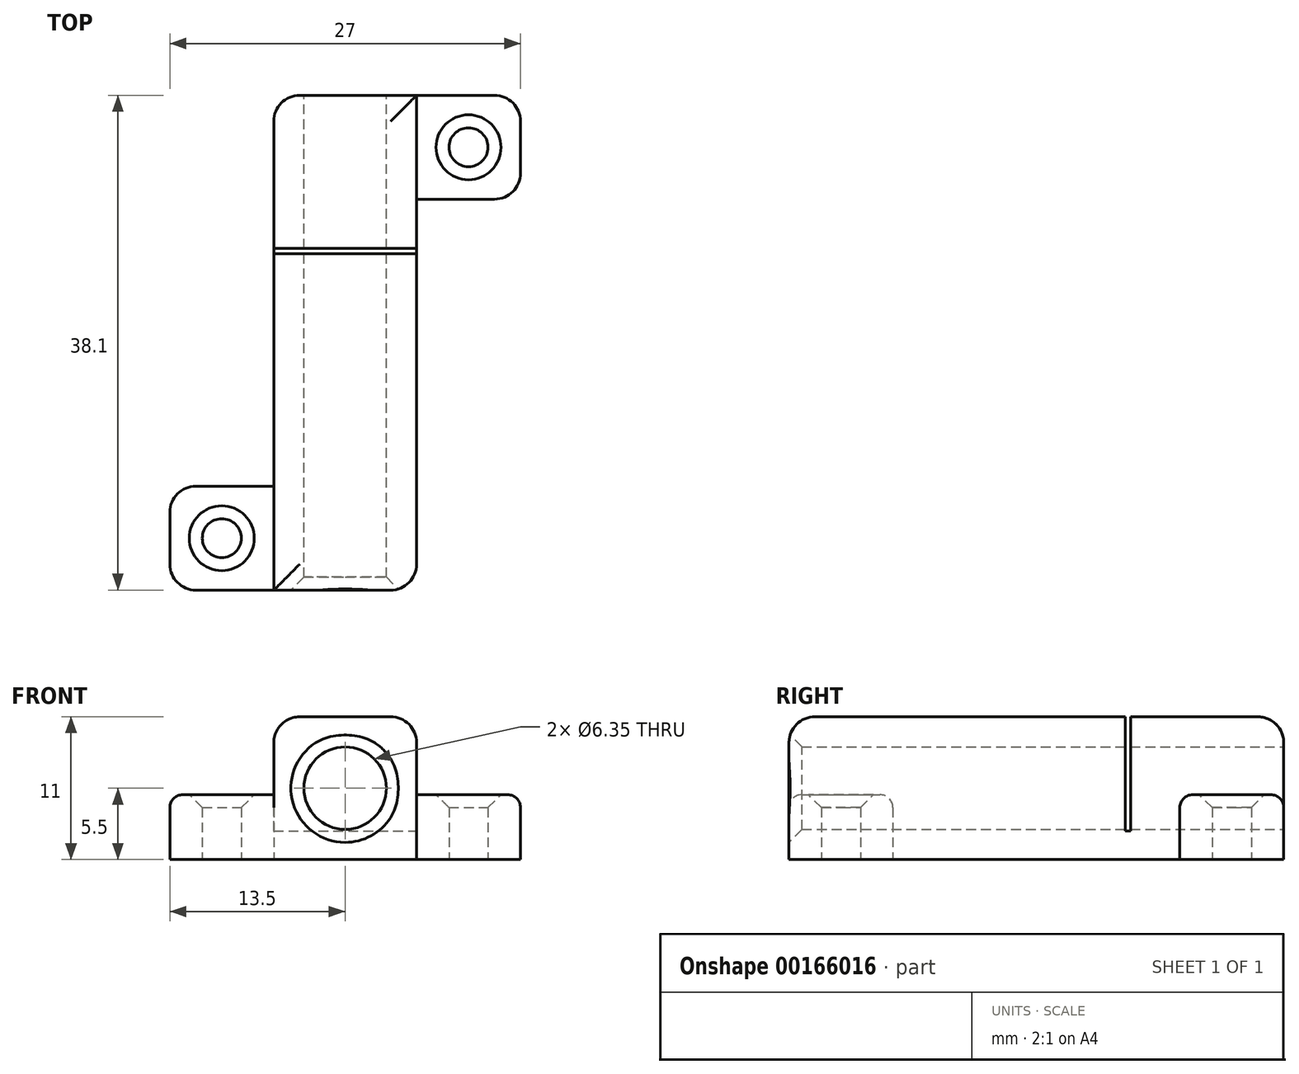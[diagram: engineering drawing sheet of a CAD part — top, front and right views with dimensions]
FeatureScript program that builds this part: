
annotation { "Feature Type Name" : "Feature", "Feature Type Description" : "" }
export const myFeature = defineFeature(function(context is Context, id is Id, definition is map)
    precondition{}
    {
        {
            var Q0;
            Q0=qCreatedBy(makeId("Front.planeOp"),FACE);
            var sketch = newSketch(context, id + "F0", { "sketchPlane" : qUnion([Q0])});
            skLineSegment(sketch, "E0.bottom", {"start": v(-5.5, 0) * mm, "end": v(5.5, 0) * mm});
            skLineSegment(sketch, "E0.top", {"start": v(-5.5, 11) * mm, "end": v(5.5, 11) * mm});
            skLineSegment(sketch, "E0.left", {"start": v(-5.5, 0) * mm, "end": v(-5.5, 11) * mm});
            skLineSegment(sketch, "E0.right", {"start": v(5.5, 0) * mm, "end": v(5.5, 11) * mm});
            skCircle(sketch, "E1", {"center": v(0, 5.5) * mm, "radius": 3.18 * mm});
            skLineSegment(sketch, "E2", {"start": v(0, 11) * mm, "end": v(0, 5.5) * mm, "construction": true});
            skLineSegment(sketch, "E3", {"start": v(5.5, 5.5) * mm, "end": v(0, 5.5) * mm, "construction": true});
            skSolve(sketch);
        }
        {
            var Q0;
            Q0=makeQuery(id+"F0.imprint","IMPRINT",FACE,{"disambiguationData":[TD([[makeQuery(id+"F0.imprint","IMPRINT",EDGE,{"derivedFrom":sQuery(id+"F0.wireOp",EDGE,"E0.bottom")}),1.0]])]});
            extrude(context, id + "F1", {"entities" : qUnion([Q0]), "depth" : 38.1 * mm});
        }
        {
            var Q0;
            Q0=makeQuery(id+"F1.opExtrude","SWEPT_FACE",FACE,{"disambiguationData":[OSD([sQuery(id+"F0.wireOp",EDGE,"E0.bottom")])]});
            var sketch = newSketch(context, id + "F2", { "sketchPlane" : qUnion([Q0])});
            skLineSegment(sketch, "E4.0.0", {"start": v(-5.5, 0) * mm, "end": v(5.5, 0) * mm});
            skLineSegment(sketch, "E4.0.1", {"start": v(5.5, 0) * mm, "end": v(5.5, 38.1) * mm});
            skLineSegment(sketch, "E4.0.2", {"start": v(5.5, 38.1) * mm, "end": v(-5.5, 38.1) * mm});
            skLineSegment(sketch, "E4.0.3", {"start": v(-5.5, 38.1) * mm, "end": v(-5.5, 0) * mm});
            skLineSegment(sketch, "E5.bottom", {"start": v(-5.5, 38.1) * mm, "end": v(-13.5, 38.1) * mm});
            skLineSegment(sketch, "E5.top", {"start": v(-5.5, 30.1) * mm, "end": v(-13.5, 30.1) * mm});
            skLineSegment(sketch, "E5.left", {"start": v(-5.5, 38.1) * mm, "end": v(-5.5, 30.1) * mm});
            skLineSegment(sketch, "E5.right", {"start": v(-13.5, 38.1) * mm, "end": v(-13.5, 30.1) * mm});
            skLineSegment(sketch, "E6.bottom", {"start": v(5.5, 0) * mm, "end": v(13.5, 0) * mm});
            skLineSegment(sketch, "E6.top", {"start": v(5.5, 8) * mm, "end": v(13.5, 8) * mm});
            skLineSegment(sketch, "E6.left", {"start": v(5.5, 0) * mm, "end": v(5.5, 8) * mm});
            skLineSegment(sketch, "E6.right", {"start": v(13.5, 0) * mm, "end": v(13.5, 8) * mm});
            skCircle(sketch, "E7", {"center": v(-9.5, 34.1) * mm, "radius": 1.5 * mm});
            skPoint(sketch, "E7.centerSnap0", {"position": v(-5.5, 34.1) * mm});
            skCircle(sketch, "E8", {"center": v(9.5, 4) * mm, "radius": 1.5 * mm});
            skPoint(sketch, "E8.centerSnap0", {"position": v(9.5, 8) * mm});
            skLineSegment(sketch, "E9", {"start": v(9.5, 8) * mm, "end": v(9.5, 4) * mm, "construction": true});
            skLineSegment(sketch, "E10", {"start": v(13.5, 4) * mm, "end": v(9.5, 4) * mm, "construction": true});
            skPoint(sketch, "E10.startSnap0", {"position": v(13.5, 4) * mm});
            skLineSegment(sketch, "E11", {"start": v(-9.5, 38.1) * mm, "end": v(-9.5, 34.1) * mm, "construction": true});
            skLineSegment(sketch, "E12", {"start": v(-9.5, 34.1) * mm, "end": v(-13.5, 34.1) * mm, "construction": true});
            skSolve(sketch);
        }
        {
            var Q0;
            Q0=makeQuery(id+"F1.opExtrude","SWEPT_FACE",FACE,{"disambiguationData":[OSD([sQuery(id+"F0.wireOp",EDGE,"E0.top")])]});
            var sketch = newSketch(context, id + "F3", { "sketchPlane" : qUnion([Q0])});
            skLineSegment(sketch, "E13.bottom", {"start": v(-5.5, -11.8) * mm, "end": v(5.5, -11.8) * mm});
            skLineSegment(sketch, "E13.top", {"start": v(-5.5, -12.2) * mm, "end": v(5.5, -12.2) * mm});
            skLineSegment(sketch, "E13.left", {"start": v(-5.5, -11.8) * mm, "end": v(-5.5, -12.2) * mm});
            skLineSegment(sketch, "E13.right", {"start": v(5.5, -11.8) * mm, "end": v(5.5, -12.2) * mm});
            skSolve(sketch);
        }
        {
            var Q0;
            Q0=makeQuery(id+"F3.imprint","IMPRINT",FACE,{"disambiguationData":[TD([[makeQuery(id+"F3.imprint","IMPRINT",EDGE,{"derivedFrom":sQuery(id+"F3.wireOp",EDGE,"E13.bottom")}),-1.0]])]});
            extrude(context, id + "F4", {"entities" : qUnion([Q0]), "operationType" : NewBodyOperationType.REMOVE, "oppositeDirection" : true, "depth" : 8.8 * mm});
        }
        {
            var Q0;
            Q0=makeQuery(id+"F2.imprint","IMPRINT",FACE,{"disambiguationData":[TD([[makeQuery(id+"F2.imprint","IMPRINT",EDGE,{"derivedFrom":sQuery(id+"F2.wireOp",EDGE,"E5.bottom")}),1.0]])]});
            var Q1;
            Q1=makeQuery(id+"F2.imprint","IMPRINT",FACE,{"disambiguationData":[TD([[makeQuery(id+"F2.imprint","IMPRINT",EDGE,{"derivedFrom":sQuery(id+"F2.wireOp",EDGE,"E6.bottom")}),1.0]])]});
            extrude(context, id + "F5", {"entities" : qUnion([Q0, Q1]), "operationType" : NewBodyOperationType.ADD, "oppositeDirection" : true, "depth" : 5 * mm});
        }
        {
            var Q0;
            Q0=makeQuery(id+"F1.opExtrude","CAP_EDGE",EDGE,{"disambiguationData":[OSD([sQuery(id+"F0.wireOp",EDGE,"E1")])],"isStart":false});
            chamfer(context, id + "F6", {"entities" : qUnion([Q0]), "width" : 1 * mm, "tangentPropagation" : true});
        }
        {
            var Q0;
            Q0=makeQuery(id+"F1.opExtrude","SWEPT_EDGE",EDGE,{"disambiguationData":[OSD([sQuery(id+"F0.wireOp",EDGE,"E0.top"),sQuery(id+"F0.wireOp",EDGE,"E0.right")])]});
            var Q1;
            Q1=makeQuery(id+"F1.opExtrude","SWEPT_EDGE",EDGE,{"disambiguationData":[OSD([sQuery(id+"F0.wireOp",EDGE,"E0.top"),sQuery(id+"F0.wireOp",EDGE,"E0.left")])]});
            var Q2;
            Q2=makeQuery(id+"F1.opExtrude","CAP_EDGE",EDGE,{"disambiguationData":[OSD([sQuery(id+"F0.wireOp",EDGE,"E0.top")])],"isStart":true});
            var Q3;
            Q3=makeQuery(id+"F5.opExtrude","CAP_EDGE",EDGE,{"disambiguationData":[OSD([sQuery(id+"F2.wireOp",EDGE,"E6.left")])],"isStart":false});
            var Q4;
            Q4=makeQuery(id+"F5.opExtrude","CAP_EDGE",EDGE,{"disambiguationData":[OSD([sQuery(id+"F2.wireOp",EDGE,"E5.left")])],"isStart":false});
            var Q5;
            Q5=makeQuery(id+"F1.opExtrude","CAP_EDGE",EDGE,{"disambiguationData":[OSD([sQuery(id+"F0.wireOp",EDGE,"E0.top")])],"isStart":false});
            var Q6;
            Q6=makeQuery(id+"F5.opExtrude","SWEPT_EDGE",EDGE,{"disambiguationData":[OSD([sQuery(id+"F2.wireOp",EDGE,"E5.bottom"),sQuery(id+"F2.wireOp",EDGE,"E5.right")])]});
            var Q7;
            Q7=makeQuery(id+"F5.opExtrude","SWEPT_EDGE",EDGE,{"disambiguationData":[OSD([sQuery(id+"F2.wireOp",EDGE,"E5.top"),sQuery(id+"F2.wireOp",EDGE,"E5.right")])]});
            var Q8;
            Q8=makeQuery(id+"F5.opExtrude","SWEPT_EDGE",EDGE,{"disambiguationData":[OSD([sQuery(id+"F2.wireOp",EDGE,"E6.bottom"),sQuery(id+"F2.wireOp",EDGE,"E6.right")])]});
            var Q9;
            Q9=makeQuery(id+"F5.opExtrude","SWEPT_EDGE",EDGE,{"disambiguationData":[OSD([sQuery(id+"F2.wireOp",EDGE,"E6.top"),sQuery(id+"F2.wireOp",EDGE,"E6.right")])]});
            var Q10;
            Q10=makeQuery(id+"F1.opExtrude","CAP_EDGE",EDGE,{"disambiguationData":[OSD([sQuery(id+"F0.wireOp",EDGE,"E0.right")])],"isStart":false});
            var Q11;
            Q11=makeQuery(id+"F1.opExtrude","CAP_EDGE",EDGE,{"disambiguationData":[OSD([sQuery(id+"F0.wireOp",EDGE,"E0.left")])],"isStart":true});
            var Q12;
            Q12=makeQuery(id+"F5.opExtrude","SWEPT_EDGE",EDGE,{"disambiguationData":[OSD([sQuery(id+"F2.wireOp",EDGE,"E4.0.3"),sQuery(id+"F2.wireOp",EDGE,"E5.top"),sQuery(id+"F2.wireOp",EDGE,"E5.left")])]});
            var Q13;
            Q13=makeQuery(id+"F5.opExtrude","SWEPT_EDGE",EDGE,{"disambiguationData":[OSD([sQuery(id+"F2.wireOp",EDGE,"E4.0.1"),sQuery(id+"F2.wireOp",EDGE,"E6.top"),sQuery(id+"F2.wireOp",EDGE,"E6.left")])]});
            fillet(context, id + "F7", {"entities" : qUnion([Q0, Q1, Q2, Q3, Q4, Q5, Q6, Q7, Q8, Q9, Q10, Q11, Q12, Q13]), "radius" : 2 * mm, "tangentPropagation" : true, "allowEdgeOverflow" : false});
        }
        {
            var Q0;
            Q0=makeQuery(id+"F5.opExtrude","CAP_EDGE",EDGE,{"disambiguationData":[OSD([sQuery(id+"F2.wireOp",EDGE,"E5.top")])],"isStart":false});
            var Q1;
            Q1=makeQuery(id+"F5.opExtrude","CAP_EDGE",EDGE,{"disambiguationData":[OSD([sQuery(id+"F2.wireOp",EDGE,"E6.top")])],"isStart":false});
            fillet(context, id + "F8", {"entities" : qUnion([Q0, Q1]), "radius" : 1 * mm, "tangentPropagation" : true, "allowEdgeOverflow" : false});
        }
        {
            var Q0;
            Q0=makeQuery(id+"F5.opExtrude","CAP_EDGE",EDGE,{"disambiguationData":[OSD([sQuery(id+"F2.wireOp",EDGE,"E7")])],"isStart":false});
            var Q1;
            Q1=makeQuery(id+"F5.opExtrude","CAP_EDGE",EDGE,{"disambiguationData":[OSD([sQuery(id+"F2.wireOp",EDGE,"E8")])],"isStart":false});
            chamfer(context, id + "F9", {"entities" : qUnion([Q0, Q1]), "width" : 1 * mm, "tangentPropagation" : true});
        }
    });
